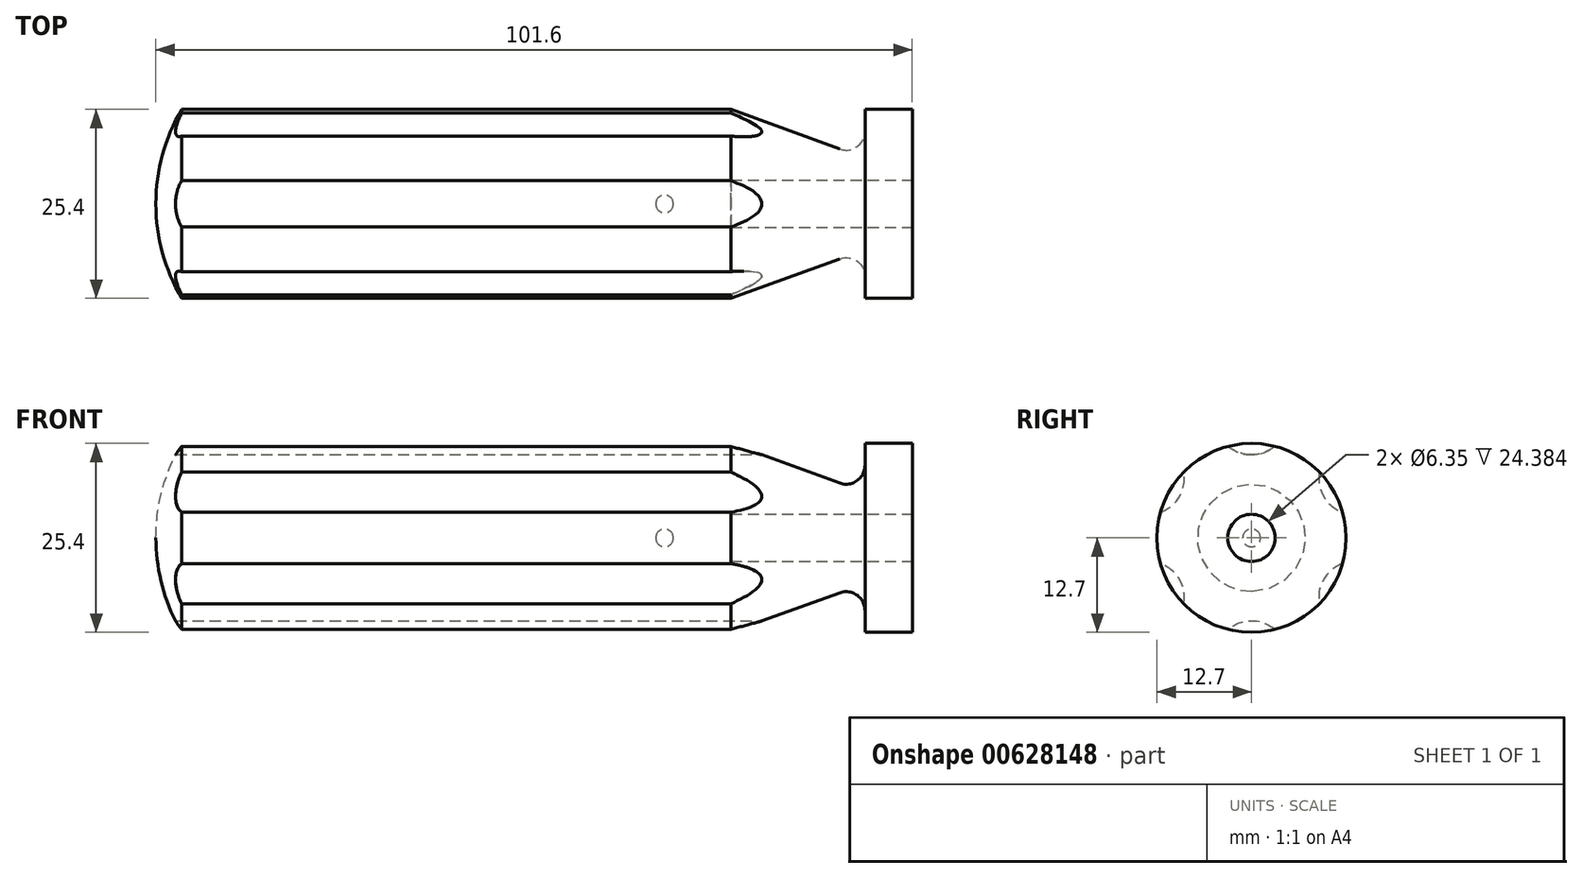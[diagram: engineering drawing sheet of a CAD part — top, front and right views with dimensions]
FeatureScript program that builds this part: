
annotation { "Feature Type Name" : "Feature", "Feature Type Description" : "" }
export const myFeature = defineFeature(function(context is Context, id is Id, definition is map)
    precondition{}
    {
        {
            var Q0;
            Q0=qCreatedBy(makeId("Front.planeOp"),FACE);
            var sketch = newSketch(context, id + "F0", { "sketchPlane" : qUnion([Q0])});
            skLineSegment(sketch, "E0.bottom", {"start": v(8.89, 0) * mm, "end": v(-68.33, 0) * mm});
            skLineSegment(sketch, "E0.top", {"start": v(33.27, 12.7) * mm, "end": v(26.92, 12.7) * mm});
            skLineSegment(sketch, "E0.left", {"start": v(33.27, 3.18) * mm, "end": v(33.27, 12.7) * mm});
            skArc(sketch, "E1", {"start": v(-64.87, 12.7) * mm, "mid": v(-67.45, 6.58) * mm, "end": v(-68.33, 0) * mm});
            skLineSegment(sketch, "E2", {"start": v(26.92, 12.7) * mm, "end": v(26.92, 9.76) * mm});
            skLineSegment(sketch, "E3", {"start": v(23.52, 7.38) * mm, "end": v(8.89, 12.7) * mm});
            skLineSegment(sketch, "E4.trimOffspring", {"start": v(8.89, 12.7) * mm, "end": v(-64.87, 12.7) * mm});
            skPoint(sketch, "E5.visualSharp", {"position": v(26.92, 6.14) * mm});
            skArc(sketch, "E5.filletArc", {"start": v(23.52, 7.38) * mm, "mid": v(25.84, 7.68) * mm, "end": v(26.92, 9.76) * mm});
            skLineSegment(sketch, "E6.top", {"start": v(33.27, 3.18) * mm, "end": v(8.89, 3.18) * mm});
            skLineSegment(sketch, "E6.right", {"start": v(8.89, 0) * mm, "end": v(8.89, 3.18) * mm});
            skCircle(sketch, "E7", {"center": v(0, 0) * mm, "radius": 1.2 * mm});
            skSolve(sketch);
        }
        {
            var Q0;
            Q0 = qSketchRegion(id + "F0", true);
            var Q1;
            Q1=sQuery(id+"F0.wireOp",EDGE,"E0.bottom");
            revolve(context, id + "F1", {"entities" : qUnion([Q0]), "axis" : qUnion([Q1]), "revolveType" : RevolveType.FULL});
        }
        {
            var Q0;
            Q0 = qSketchRegion(id + "F0", true);
            var Q1;
            Q1=sQuery(id+"F0.wireOp",EDGE,"E0.bottom");
            revolve(context, id + "F2", {"entities" : qUnion([Q0]), "axis" : qUnion([Q1]), "revolveType" : RevolveType.FULL});
        }
        {
            var Q0;
            Q0=makeQuery(id+"F1.opRevolve","SWEPT_FACE",FACE,{"disambiguationData":[OSD([sQuery(id+"F0.wireOp",EDGE,"E0.left")])]});
            var sketch = newSketch(context, id + "F3", { "sketchPlane" : qUnion([Q0])});
            skCircle(sketch, "E8", {"center": v(0, 0) * mm, "radius": 16 * mm, "construction": true});
            skCircle(sketch, "E9", {"center": v(0, 16) * mm, "radius": 4.83 * mm});
            skCircle(sketch, "E10.1.0", {"center": v(-13.86, 8) * mm, "radius": 4.83 * mm});
            skCircle(sketch, "E10.2.0", {"center": v(-13.86, -8) * mm, "radius": 4.83 * mm});
            skCircle(sketch, "E10.3.0", {"center": v(0, -16) * mm, "radius": 4.83 * mm});
            skCircle(sketch, "E10.4.0", {"center": v(13.86, -8) * mm, "radius": 4.83 * mm});
            skCircle(sketch, "E10.5.0", {"center": v(13.86, 8) * mm, "radius": 4.83 * mm});
            skSolve(sketch);
        }
        {
            var Q0;
            Q0 = qSketchRegion(id + "F3", true);
            extrude(context, id + "F4", {"entities" : qUnion([Q0]), "operationType" : NewBodyOperationType.REMOVE, "oppositeDirection" : true, "depth" : 101.6 * mm, "offsetDistance" : 25.4 * mm, "hasSecondDirection" : true, "secondDirectionOppositeDirection" : true, "secondDirectionDepth" : 6.35 * mm});
        }
    });
